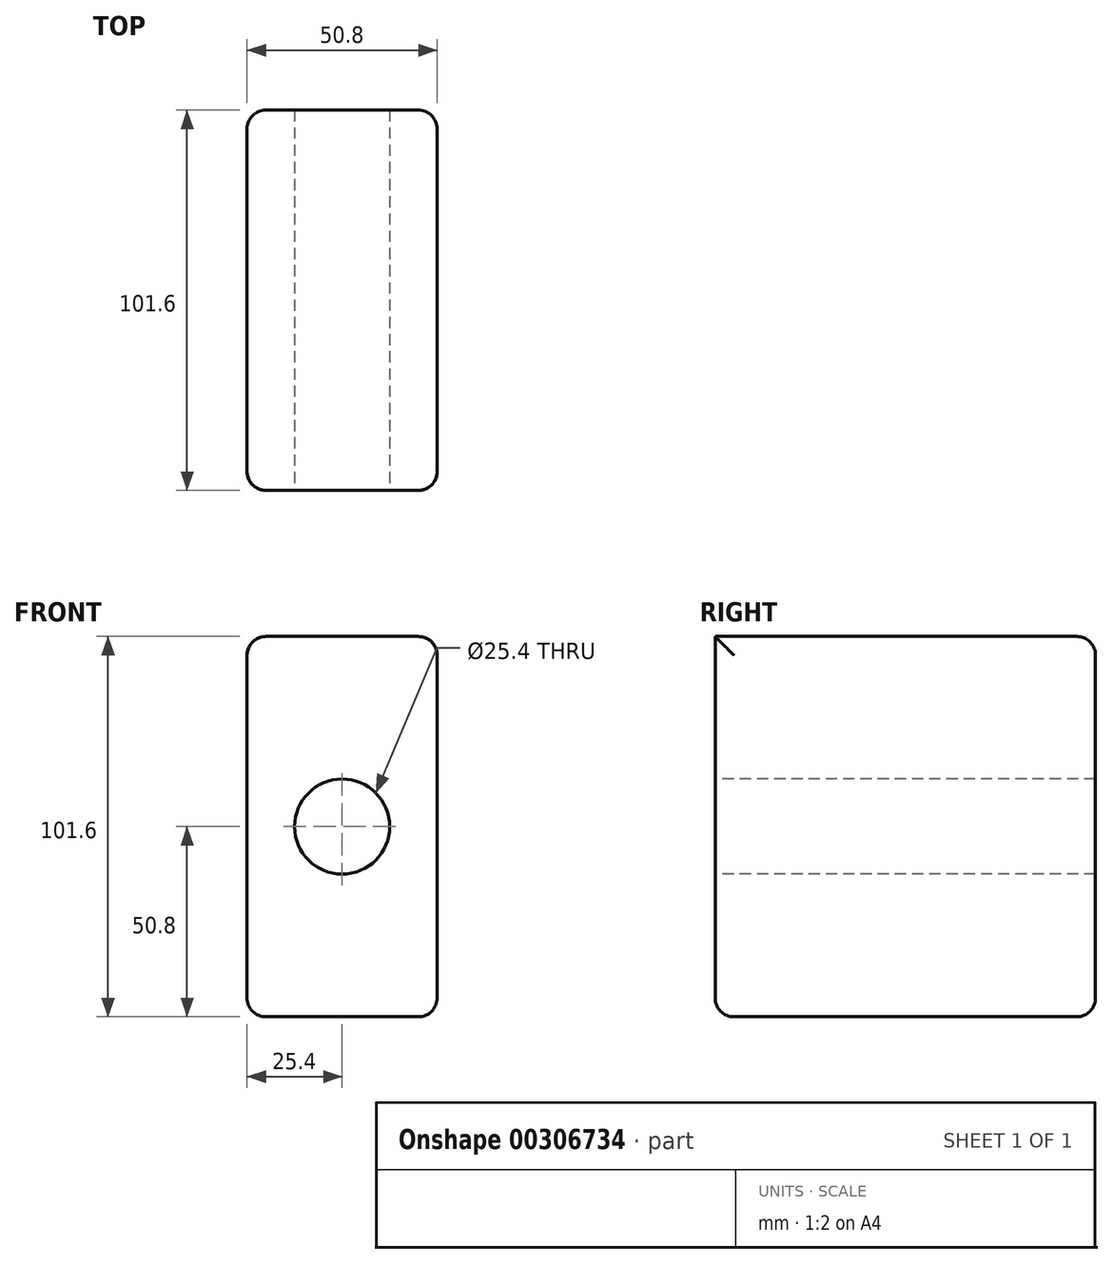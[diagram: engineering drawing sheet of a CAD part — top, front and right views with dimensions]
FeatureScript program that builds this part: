
annotation { "Feature Type Name" : "Feature", "Feature Type Description" : "" }
export const myFeature = defineFeature(function(context is Context, id is Id, definition is map)
    precondition{}
    {
        {
            var Q0;
            Q0=qCreatedBy(makeId("Front.planeOp"),FACE);
            var sketch = newSketch(context, id + "F0", { "sketchPlane" : qUnion([Q0])});
            skLineSegment(sketch, "E0.bottom", {"start": v(25.4, 50.8) * mm, "end": v(-25.4, 50.8) * mm});
            skLineSegment(sketch, "E0.top", {"start": v(25.4, -50.8) * mm, "end": v(-25.4, -50.8) * mm});
            skLineSegment(sketch, "E0.left", {"start": v(25.4, 50.8) * mm, "end": v(25.4, -50.8) * mm});
            skLineSegment(sketch, "E0.right", {"start": v(-25.4, 50.8) * mm, "end": v(-25.4, -50.8) * mm});
            skPoint(sketch, "E0.middle", {"position": v(0, 0) * mm});
            skSolve(sketch);
        }
        {
            var Q0;
            Q0=makeQuery(id+"F0.imprint","IMPRINT",FACE,{"disambiguationData":[TD([[makeQuery(id+"F0.imprint","IMPRINT",EDGE,{"derivedFrom":sQuery(id+"F0.wireOp",EDGE,"E0.bottom")}),1.0]])]});
            extrude(context, id + "F1", {"entities" : qUnion([Q0]), "oppositeDirection" : true, "depth" : 101.6 * mm});
        }
        {
            var Q0;
            Q0=qCreatedBy(makeId("Front.planeOp"),FACE);
            var sketch = newSketch(context, id + "F2", { "sketchPlane" : qUnion([Q0])});
            skCircle(sketch, "E1", {"center": v(0, 0) * mm, "radius": 12.7 * mm});
            skSolve(sketch);
        }
        {
            var Q0;
            Q0=makeQuery(id+"F2.imprint","IMPRINT",FACE,{"disambiguationData":[TD([[makeQuery(id+"F2.imprint","IMPRINT",EDGE,{"derivedFrom":sQuery(id+"F2.wireOp",EDGE,"E1")}),1.0]])]});
            var Q1;
            Q1=makeQuery(id+"F1.opExtrude","CAP_FACE",FACE,{"disambiguationData":[OSD([sQuery(id+"F0.wireOp",EDGE,"E0.bottom"),sQuery(id+"F0.wireOp",EDGE,"E0.top"),sQuery(id+"F0.wireOp",EDGE,"E0.left"),sQuery(id+"F0.wireOp",EDGE,"E0.right")])],"isStart":false});
            extrude(context, id + "F3", {"entities" : qUnion([Q0]), "operationType" : NewBodyOperationType.REMOVE, "endBound" : BoundingType.UP_TO_SURFACE, "oppositeDirection" : true, "endBoundEntityFace" : qUnion([Q1]), "depth" : 25.4 * mm});
        }
        {
            var Q0;
            Q0=makeQuery(id+"F1.opExtrude","SWEPT_EDGE",EDGE,{"disambiguationData":[OSD([sQuery(id+"F0.wireOp",EDGE,"E0.bottom"),sQuery(id+"F0.wireOp",EDGE,"E0.left")])]});
            var Q1;
            Q1=makeQuery(id+"F1.opExtrude","SWEPT_EDGE",EDGE,{"disambiguationData":[OSD([sQuery(id+"F0.wireOp",EDGE,"E0.bottom"),sQuery(id+"F0.wireOp",EDGE,"E0.right")])]});
            var Q2;
            Q2=makeQuery(id+"F1.opExtrude","SWEPT_EDGE",EDGE,{"disambiguationData":[OSD([sQuery(id+"F0.wireOp",EDGE,"E0.top"),sQuery(id+"F0.wireOp",EDGE,"E0.left")])]});
            var Q3;
            Q3=makeQuery(id+"F1.opExtrude","SWEPT_EDGE",EDGE,{"disambiguationData":[OSD([sQuery(id+"F0.wireOp",EDGE,"E0.top"),sQuery(id+"F0.wireOp",EDGE,"E0.right")])]});
            var Q4;
            Q4=makeQuery(id+"F1.opExtrude","CAP_EDGE",EDGE,{"disambiguationData":[OSD([sQuery(id+"F0.wireOp",EDGE,"E0.top")])],"isStart":false});
            var Q5;
            Q5=makeQuery(id+"F1.opExtrude","CAP_EDGE",EDGE,{"disambiguationData":[OSD([sQuery(id+"F0.wireOp",EDGE,"E0.right")])],"isStart":false});
            var Q6;
            Q6=makeQuery(id+"F1.opExtrude","CAP_EDGE",EDGE,{"disambiguationData":[OSD([sQuery(id+"F0.wireOp",EDGE,"E0.bottom")])],"isStart":false});
            var Q7;
            Q7=makeQuery(id+"F1.opExtrude","CAP_EDGE",EDGE,{"disambiguationData":[OSD([sQuery(id+"F0.wireOp",EDGE,"E0.left")])],"isStart":false});
            var Q8;
            Q8=makeQuery(id+"F1.opExtrude","CAP_EDGE",EDGE,{"disambiguationData":[OSD([sQuery(id+"F0.wireOp",EDGE,"E0.left")])],"isStart":true});
            var Q9;
            Q9=makeQuery(id+"F1.opExtrude","CAP_EDGE",EDGE,{"disambiguationData":[OSD([sQuery(id+"F0.wireOp",EDGE,"E0.right")])],"isStart":true});
            var Q10;
            Q10=makeQuery(id+"F1.opExtrude","CAP_EDGE",EDGE,{"disambiguationData":[OSD([sQuery(id+"F0.wireOp",EDGE,"E0.top")])],"isStart":true});
            fillet(context, id + "F4", {"entities" : qUnion([Q0, Q1, Q2, Q3, Q4, Q5, Q6, Q7, Q8, Q9, Q10]), "radius" : 5.08 * mm, "tangentPropagation" : true, "allowEdgeOverflow" : false});
        }
    });
